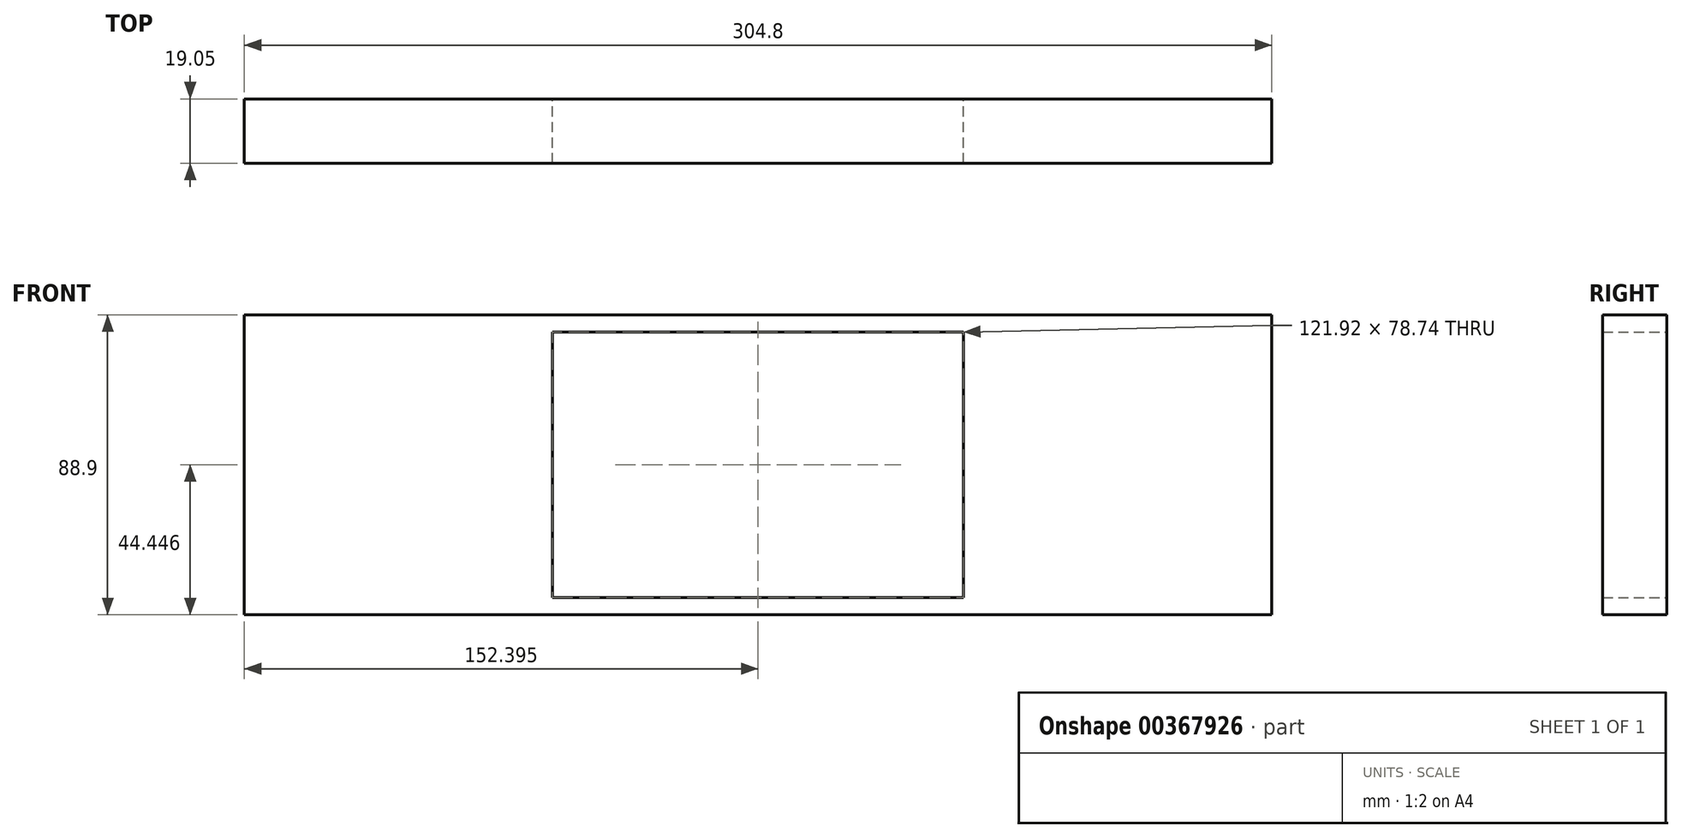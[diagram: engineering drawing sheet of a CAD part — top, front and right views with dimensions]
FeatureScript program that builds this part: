
annotation { "Feature Type Name" : "Feature", "Feature Type Description" : "" }
export const myFeature = defineFeature(function(context is Context, id is Id, definition is map)
    precondition{}
    {
        {
            var Q0;
            Q0=qCreatedBy(makeId("Front.planeOp"),FACE);
            var sketch = newSketch(context, id + "F0", { "sketchPlane" : qUnion([Q0])});
            skLineSegment(sketch, "E0.bottom", {"start": v(-142.35, 78) * mm, "end": v(162.45, 78) * mm});
            skLineSegment(sketch, "E0.top", {"start": v(-142.35, -10.9) * mm, "end": v(162.45, -10.9) * mm});
            skLineSegment(sketch, "E0.left", {"start": v(-142.35, 78) * mm, "end": v(-142.35, -10.9) * mm});
            skLineSegment(sketch, "E0.right", {"start": v(162.45, 78) * mm, "end": v(162.45, -10.9) * mm});
            skLineSegment(sketch, "E1.bottom", {"start": v(-50.91, 72.93) * mm, "end": v(71, 72.93) * mm});
            skLineSegment(sketch, "E1.top", {"start": v(-50.91, -5.81) * mm, "end": v(71, -5.81) * mm});
            skLineSegment(sketch, "E1.left", {"start": v(-50.91, 72.93) * mm, "end": v(-50.91, -5.81) * mm});
            skLineSegment(sketch, "E1.right", {"start": v(71, 72.93) * mm, "end": v(71, -5.81) * mm});
            skSolve(sketch);
        }
        {
            var Q0;
            Q0=makeQuery(id+"F0.imprint","IMPRINT",FACE,{"disambiguationData":[TD([[makeQuery(id+"F0.imprint","IMPRINT",EDGE,{"derivedFrom":sQuery(id+"F0.wireOp",EDGE,"E0.bottom")}),-1.0]])]});
            extrude(context, id + "F1", {"entities" : qUnion([Q0]), "depth" : 19.05 * mm});
        }
    });
